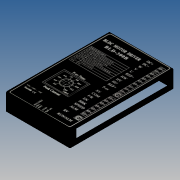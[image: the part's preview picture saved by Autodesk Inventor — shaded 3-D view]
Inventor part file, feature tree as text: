
AUTODESK INVENTOR PART (.ipt)
format: ipt  version: 2018.2 (Build 222227000, 227)  size: 148,480 bytes
history: native  units: mm
features: extrude x3, sketch x3, fillet x1
ambient origin geometry x8: Origin, YZ Plane, XZ Plane, XY Plane, X Axis, Y Axis, Z Axis, Center Point
bodies: Body1 (feature_tree)
feature tree (7):
  extrude  "Grundkörper"  Depth=126.0mm
  extrude  "Ausschnitt"  Depth=1.0mm
  extrude  "Anschlüsse"  Depth=20.0mm TaperAngle=0.0deg
  fillet  "Rundung2"  Radius=7.5mm
  sketch  "Skizze1"  dims[d23=77.5mm d24=126.0mm]
  sketch  "Skizze6"  dims[d25=21.0mm d26=0.0mm d27=1.0mm]
  sketch  "Skizze8"  dims[d28=1.0mm d29=20.0mm d30=0.0mm d32=7.5mm d33=6.0mm d34=4.0mm d35=20.0mm d36=0.0mm d37=1.0mm]
